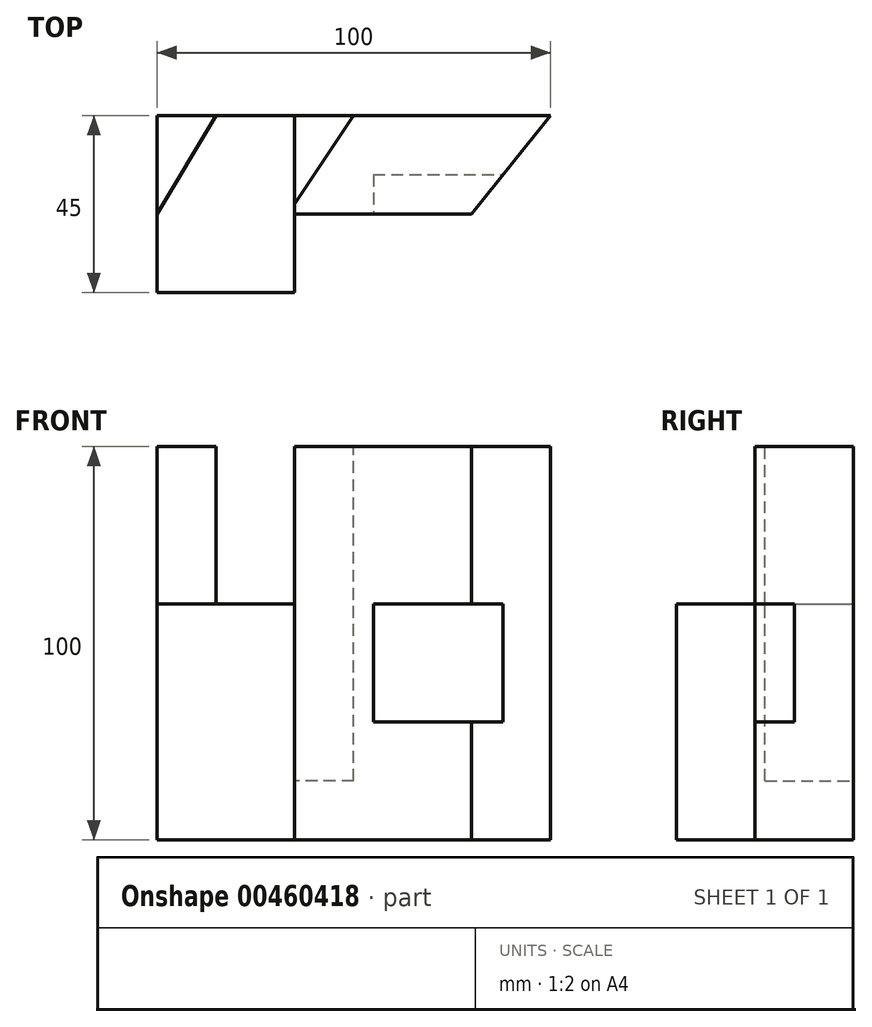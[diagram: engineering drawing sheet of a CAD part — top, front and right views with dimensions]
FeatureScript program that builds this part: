
annotation { "Feature Type Name" : "Feature", "Feature Type Description" : "" }
export const myFeature = defineFeature(function(context is Context, id is Id, definition is map)
    precondition{}
    {
        {
            var Q0;
            Q0=qCreatedBy(makeId("Front.planeOp"),FACE);
            var sketch = newSketch(context, id + "F0", { "sketchPlane" : qUnion([Q0])});
            skLineSegment(sketch, "E0.bottom", {"start": v(0, 0) * mm, "end": v(-100, 0) * mm});
            skLineSegment(sketch, "E0.top", {"start": v(0, 100) * mm, "end": v(-100, 100) * mm});
            skLineSegment(sketch, "E0.left", {"start": v(0, 0) * mm, "end": v(0, 100) * mm});
            skLineSegment(sketch, "E0.right", {"start": v(-100, 0) * mm, "end": v(-100, 100) * mm});
            skSolve(sketch);
        }
        {
            var Q0;
            Q0 = qSketchRegion(id + "F0", true);
            extrude(context, id + "F1", {"entities" : qUnion([Q0]), "depth" : 45 * mm});
        }
        {
            var Q0;
            Q0=makeQuery(id+"F1.opExtrude","SWEPT_FACE",FACE,{"disambiguationData":[OSD([sQuery(id+"F0.wireOp",EDGE,"E0.top")])]});
            var sketch = newSketch(context, id + "F2", { "sketchPlane" : qUnion([Q0])});
            skLineSegment(sketch, "E1", {"start": v(-100, -45) * mm, "end": v(-65, -45) * mm});
            skLineSegment(sketch, "E2", {"start": v(-65, -45) * mm, "end": v(-65, 0) * mm});
            skLineSegment(sketch, "E3", {"start": v(-100, 0) * mm, "end": v(-100, -25) * mm});
            skLineSegment(sketch, "E4", {"start": v(-100, -25) * mm, "end": v(-85, 0) * mm});
            skLineSegment(sketch, "E5", {"start": v(-85, 0) * mm, "end": v(-100, 0) * mm});
            skSolve(sketch);
        }
        {
            var Q0;
            {var subQ1=sQuery(id+"F2.wireOp",EDGE,"E1");Q0=makeQuery(id+"F2.imprint","IMPRINT",FACE,{"disambiguationData":[TD([[makeQuery(id+"F2.imprint","IMPRINT",EDGE,{"derivedFrom":subQ1}),-1.0]])]});}
            extrude(context, id + "F3", {"entities" : qUnion([Q0]), "operationType" : NewBodyOperationType.REMOVE, "oppositeDirection" : true, "depth" : 40 * mm});
        }
        {
            var Q0;
            {var subQ1=sQuery(id+"F0.wireOp",EDGE,"E0.left");var subQ2=sQuery(id+"F0.wireOp",EDGE,"E0.top");Q0=makeQuery(id+"F3.boolean.opBoolean","SPLIT",FACE,{"disambiguationData":[TD([makeQuery(id+"F1.opExtrude","SWEPT_FACE",FACE,{"disambiguationData":[OSD([subQ1])]})])],"derivedFrom":makeQuery(id+"F1.opExtrude","SWEPT_FACE",FACE,{"disambiguationData":[OSD([subQ2])]})});}
            var sketch = newSketch(context, id + "F4", { "sketchPlane" : qUnion([Q0])});
            skLineSegment(sketch, "E6", {"start": v(-65, 0) * mm, "end": v(-65, -22.5) * mm});
            skLineSegment(sketch, "E7", {"start": v(-65, -22.5) * mm, "end": v(-50, 0) * mm});
            skLineSegment(sketch, "E8", {"start": v(-50, 0) * mm, "end": v(-65, 0) * mm});
            skSolve(sketch);
        }
        {
            var Q0;
            Q0=makeQuery(id+"F4.imprint","IMPRINT",FACE,{"disambiguationData":[TD([[makeQuery(id+"F4.imprint","IMPRINT",EDGE,{"derivedFrom":sQuery(id+"F4.wireOp",EDGE,"E6")}),-1.0]])]});
            extrude(context, id + "F5", {"entities" : qUnion([Q0]), "operationType" : NewBodyOperationType.REMOVE, "oppositeDirection" : true, "depth" : 85 * mm});
        }
        {
            var Q0;
            {var subQ1=sQuery(id+"F0.wireOp",EDGE,"E0.left");var subQ2=sQuery(id+"F0.wireOp",EDGE,"E0.top");Q0=makeQuery(id+"F3.boolean.opBoolean","SPLIT",FACE,{"disambiguationData":[TD([makeQuery(id+"F1.opExtrude","SWEPT_FACE",FACE,{"disambiguationData":[OSD([subQ1])]})])],"derivedFrom":makeQuery(id+"F1.opExtrude","SWEPT_FACE",FACE,{"disambiguationData":[OSD([subQ2])]})});}
            var sketch = newSketch(context, id + "F6", { "sketchPlane" : qUnion([Q0])});
            skLineSegment(sketch, "E9", {"start": v(-65, -45) * mm, "end": v(-65, -25) * mm});
            skLineSegment(sketch, "E10", {"start": v(-65, -25) * mm, "end": v(-20, -25) * mm});
            skLineSegment(sketch, "E11", {"start": v(-20, -25) * mm, "end": v(-20, -45) * mm});
            skLineSegment(sketch, "E12", {"start": v(-20, -45) * mm, "end": v(-65, -45) * mm});
            skSolve(sketch);
        }
        {
            var Q0;
            Q0 = qSketchRegion(id + "F6", true);
            extrude(context, id + "F7", {"entities" : qUnion([Q0]), "operationType" : NewBodyOperationType.REMOVE, "endBound" : BoundingType.THROUGH_ALL, "oppositeDirection" : true, "depth" : 25 * mm});
        }
        {
            var Q0;
            {var subQ1=sQuery(id+"F0.wireOp",EDGE,"E0.left");var subQ2=sQuery(id+"F0.wireOp",EDGE,"E0.top");Q0=makeQuery(id+"F3.boolean.opBoolean","SPLIT",FACE,{"disambiguationData":[TD([makeQuery(id+"F1.opExtrude","SWEPT_FACE",FACE,{"disambiguationData":[OSD([subQ1])]})])],"derivedFrom":makeQuery(id+"F1.opExtrude","SWEPT_FACE",FACE,{"disambiguationData":[OSD([subQ2])]})});}
            var sketch = newSketch(context, id + "F8", { "sketchPlane" : qUnion([Q0])});
            skLineSegment(sketch, "E13", {"start": v(-20, -25) * mm, "end": v(0, 0) * mm});
            skSolve(sketch);
        }
        {
            var Q0;
            Q0=makeQuery(id+"F8.imprint","IMPRINT",FACE,{"disambiguationData":[TD([[makeQuery(id+"F8.imprint","IMPRINT",EDGE,{"derivedFrom":sQuery(id+"F8.wireOp",EDGE,"E13")}),-1.0]])]});
            extrude(context, id + "F9", {"entities" : qUnion([Q0]), "operationType" : NewBodyOperationType.REMOVE, "endBound" : BoundingType.THROUGH_ALL, "oppositeDirection" : true, "depth" : 25 * mm});
        }
        {
            var Q0;
            Q0=makeQuery(id+"F7.boolean.opBoolean","COPY",FACE,{"derivedFrom":makeQuery(id+"F7.opExtrude","SWEPT_FACE",FACE,{"disambiguationData":[OSD([sQuery(id+"F6.wireOp",EDGE,"E10")])]})});
            var sketch = newSketch(context, id + "F10", { "sketchPlane" : qUnion([Q0])});
            skLineSegment(sketch, "E14", {"start": v(-65, 0) * mm, "end": v(-45, 0) * mm});
            skLineSegment(sketch, "E15", {"start": v(-45, 0) * mm, "end": v(-45, 30) * mm});
            skLineSegment(sketch, "E16", {"start": v(-45, 30) * mm, "end": v(-45, 60) * mm});
            skLineSegment(sketch, "E17", {"start": v(-45, 60) * mm, "end": v(-10, 60) * mm});
            skLineSegment(sketch, "E18", {"start": v(-10, 60) * mm, "end": v(-10, 30) * mm});
            skLineSegment(sketch, "E19", {"start": v(-10, 30) * mm, "end": v(-45, 30) * mm});
            skSolve(sketch);
        }
        {
            var Q0;
            {var subQ0=sQuery(id+"F10.wireOp",EDGE,"E16");Q0=makeQuery(id+"F10.imprint","IMPRINT",FACE,{"disambiguationData":[TD([[makeQuery(id+"F10.imprint","IMPRINT",EDGE,{"derivedFrom":subQ0}),-1.0]])]});}
            var Q1;
            {var subQ0=sQuery(id+"F10.wireOp",EDGE,"E18");Q1=makeQuery(id+"F10.imprint","IMPRINT",FACE,{"disambiguationData":[TD([[makeQuery(id+"F10.imprint","IMPRINT",EDGE,{"derivedFrom":subQ0}),-1.0]])]});}
            extrude(context, id + "F11", {"entities" : qUnion([Q0, Q1]), "operationType" : NewBodyOperationType.REMOVE, "oppositeDirection" : true, "depth" : 10 * mm});
        }
    });
